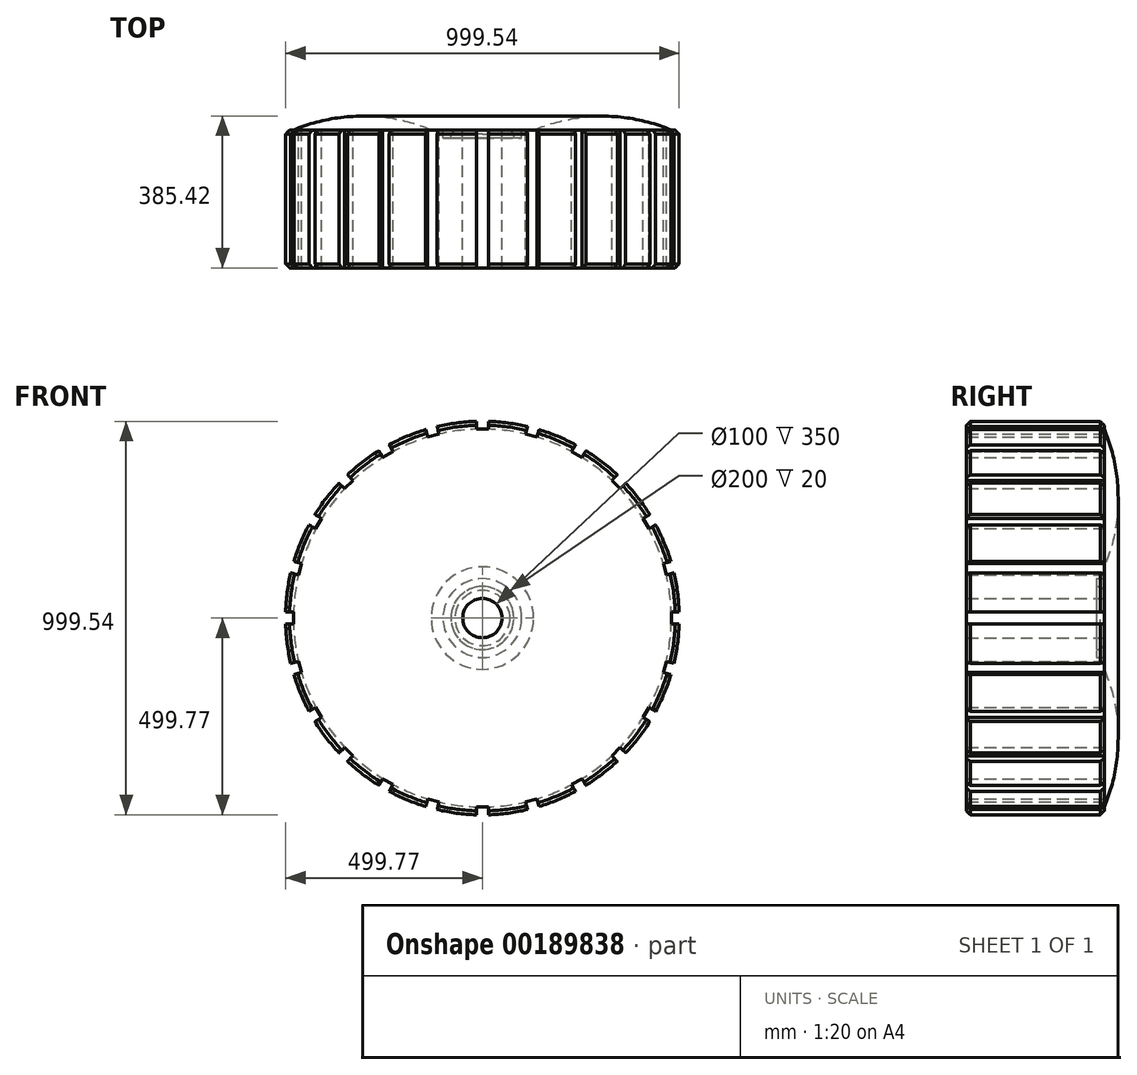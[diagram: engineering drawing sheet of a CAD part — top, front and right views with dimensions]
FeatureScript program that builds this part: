
annotation { "Feature Type Name" : "Feature", "Feature Type Description" : "" }
export const myFeature = defineFeature(function(context is Context, id is Id, definition is map)
    precondition{}
    {
        {
            var Q0;
            Q0=qCreatedBy(makeId("Front.planeOp"),FACE);
            var sketch = newSketch(context, id + "F0", { "sketchPlane" : qUnion([Q0])});
            skCircle(sketch, "E0", {"center": v(0, 0) * mm, "radius": 50 * mm});
            skCircle(sketch, "E1", {"center": v(0, 0) * mm, "radius": 500 * mm});
            skSolve(sketch);
        }
        {
            var Q0;
            Q0=makeQuery(id+"F0.imprint","IMPRINT",FACE,{"disambiguationData":[TD([[makeQuery(id+"F0.imprint","IMPRINT",EDGE,{"derivedFrom":sQuery(id+"F0.wireOp",EDGE,"E0")}),-1.0]])]});
            extrude(context, id + "F1", {"entities" : qUnion([Q0]), "depth" : 350 * mm});
        }
        {
            var Q0;
            Q0=qCreatedBy(makeId("Front.planeOp"),FACE);
            var sketch = newSketch(context, id + "F2", { "sketchPlane" : qUnion([Q0])});
            skLineSegment(sketch, "E2.bottom", {"start": v(15, 500) * mm, "end": v(-15, 500) * mm});
            skLineSegment(sketch, "E2.top", {"start": v(15, 480) * mm, "end": v(-15, 480) * mm});
            skLineSegment(sketch, "E2.left", {"start": v(15, 500) * mm, "end": v(15, 480) * mm});
            skLineSegment(sketch, "E2.right", {"start": v(-15, 500) * mm, "end": v(-15, 480) * mm});
            skLineSegment(sketch, "E3", {"start": v(0, 0) * mm, "end": v(0, 782.63) * mm, "construction": true});
            skLineSegment(sketch, "E4.1.0", {"start": v(-143.9, 479.08) * mm, "end": v(-138.72, 459.76) * mm});
            skLineSegment(sketch, "E4.1.1", {"start": v(-109.74, 467.53) * mm, "end": v(-138.72, 459.76) * mm});
            skLineSegment(sketch, "E4.1.2", {"start": v(-114.92, 486.85) * mm, "end": v(-109.74, 467.53) * mm});
            skLineSegment(sketch, "E4.1.3", {"start": v(-114.92, 486.85) * mm, "end": v(-143.9, 479.08) * mm});
            skLineSegment(sketch, "E4.2.0", {"start": v(-263, 425.51) * mm, "end": v(-253, 408.2) * mm});
            skLineSegment(sketch, "E4.2.1", {"start": v(-227, 423.2) * mm, "end": v(-253, 408.2) * mm});
            skLineSegment(sketch, "E4.2.2", {"start": v(-237, 440.51) * mm, "end": v(-227, 423.2) * mm});
            skLineSegment(sketch, "E4.2.3", {"start": v(-237, 440.51) * mm, "end": v(-263, 425.51) * mm});
            skLineSegment(sketch, "E4.3.0", {"start": v(-364.16, 342.95) * mm, "end": v(-350.02, 328.8) * mm});
            skLineSegment(sketch, "E4.3.1", {"start": v(-328.8, 350.02) * mm, "end": v(-350.02, 328.8) * mm});
            skLineSegment(sketch, "E4.3.2", {"start": v(-342.95, 364.16) * mm, "end": v(-328.8, 350.02) * mm});
            skLineSegment(sketch, "E4.3.3", {"start": v(-342.95, 364.16) * mm, "end": v(-364.16, 342.95) * mm});
            skLineSegment(sketch, "E4.4.0", {"start": v(-440.51, 237) * mm, "end": v(-423.2, 227) * mm});
            skLineSegment(sketch, "E4.4.1", {"start": v(-408.2, 253) * mm, "end": v(-423.2, 227) * mm});
            skLineSegment(sketch, "E4.4.2", {"start": v(-425.51, 263) * mm, "end": v(-408.2, 253) * mm});
            skLineSegment(sketch, "E4.4.3", {"start": v(-425.51, 263) * mm, "end": v(-440.51, 237) * mm});
            skLineSegment(sketch, "E4.5.0", {"start": v(-486.85, 114.92) * mm, "end": v(-467.53, 109.74) * mm});
            skLineSegment(sketch, "E4.5.1", {"start": v(-459.76, 138.72) * mm, "end": v(-467.53, 109.74) * mm});
            skLineSegment(sketch, "E4.5.2", {"start": v(-479.08, 143.9) * mm, "end": v(-459.76, 138.72) * mm});
            skLineSegment(sketch, "E4.5.3", {"start": v(-479.08, 143.9) * mm, "end": v(-486.85, 114.92) * mm});
            skLineSegment(sketch, "E4.6.0", {"start": v(-500, -15) * mm, "end": v(-480, -15) * mm});
            skLineSegment(sketch, "E4.6.1", {"start": v(-480, 15) * mm, "end": v(-480, -15) * mm});
            skLineSegment(sketch, "E4.6.2", {"start": v(-500, 15) * mm, "end": v(-480, 15) * mm});
            skLineSegment(sketch, "E4.6.3", {"start": v(-500, 15) * mm, "end": v(-500, -15) * mm});
            skLineSegment(sketch, "E4.7.0", {"start": v(-479.08, -143.9) * mm, "end": v(-459.76, -138.72) * mm});
            skLineSegment(sketch, "E4.7.1", {"start": v(-467.53, -109.74) * mm, "end": v(-459.76, -138.72) * mm});
            skLineSegment(sketch, "E4.7.2", {"start": v(-486.85, -114.92) * mm, "end": v(-467.53, -109.74) * mm});
            skLineSegment(sketch, "E4.7.3", {"start": v(-486.85, -114.92) * mm, "end": v(-479.08, -143.9) * mm});
            skLineSegment(sketch, "E4.8.0", {"start": v(-425.51, -263) * mm, "end": v(-408.2, -253) * mm});
            skLineSegment(sketch, "E4.8.1", {"start": v(-423.2, -227) * mm, "end": v(-408.2, -253) * mm});
            skLineSegment(sketch, "E4.8.2", {"start": v(-440.51, -237) * mm, "end": v(-423.2, -227) * mm});
            skLineSegment(sketch, "E4.8.3", {"start": v(-440.51, -237) * mm, "end": v(-425.51, -263) * mm});
            skLineSegment(sketch, "E4.9.0", {"start": v(-342.95, -364.16) * mm, "end": v(-328.8, -350.02) * mm});
            skLineSegment(sketch, "E4.9.1", {"start": v(-350.02, -328.8) * mm, "end": v(-328.8, -350.02) * mm});
            skLineSegment(sketch, "E4.9.2", {"start": v(-364.16, -342.95) * mm, "end": v(-350.02, -328.8) * mm});
            skLineSegment(sketch, "E4.9.3", {"start": v(-364.16, -342.95) * mm, "end": v(-342.95, -364.16) * mm});
            skLineSegment(sketch, "E4.10.0", {"start": v(-237, -440.51) * mm, "end": v(-227, -423.2) * mm});
            skLineSegment(sketch, "E4.10.1", {"start": v(-253, -408.2) * mm, "end": v(-227, -423.2) * mm});
            skLineSegment(sketch, "E4.10.2", {"start": v(-263, -425.51) * mm, "end": v(-253, -408.2) * mm});
            skLineSegment(sketch, "E4.10.3", {"start": v(-263, -425.51) * mm, "end": v(-237, -440.51) * mm});
            skLineSegment(sketch, "E4.11.0", {"start": v(-114.92, -486.85) * mm, "end": v(-109.74, -467.53) * mm});
            skLineSegment(sketch, "E4.11.1", {"start": v(-138.72, -459.76) * mm, "end": v(-109.74, -467.53) * mm});
            skLineSegment(sketch, "E4.11.2", {"start": v(-143.9, -479.08) * mm, "end": v(-138.72, -459.76) * mm});
            skLineSegment(sketch, "E4.11.3", {"start": v(-143.9, -479.08) * mm, "end": v(-114.92, -486.85) * mm});
            skLineSegment(sketch, "E4.12.0", {"start": v(15, -500) * mm, "end": v(15, -480) * mm});
            skLineSegment(sketch, "E4.12.1", {"start": v(-15, -480) * mm, "end": v(15, -480) * mm});
            skLineSegment(sketch, "E4.12.2", {"start": v(-15, -500) * mm, "end": v(-15, -480) * mm});
            skLineSegment(sketch, "E4.12.3", {"start": v(-15, -500) * mm, "end": v(15, -500) * mm});
            skLineSegment(sketch, "E4.13.0", {"start": v(143.9, -479.08) * mm, "end": v(138.72, -459.76) * mm});
            skLineSegment(sketch, "E4.13.1", {"start": v(109.74, -467.53) * mm, "end": v(138.72, -459.76) * mm});
            skLineSegment(sketch, "E4.13.2", {"start": v(114.92, -486.85) * mm, "end": v(109.74, -467.53) * mm});
            skLineSegment(sketch, "E4.13.3", {"start": v(114.92, -486.85) * mm, "end": v(143.9, -479.08) * mm});
            skLineSegment(sketch, "E4.14.0", {"start": v(263, -425.51) * mm, "end": v(253, -408.2) * mm});
            skLineSegment(sketch, "E4.14.1", {"start": v(227, -423.2) * mm, "end": v(253, -408.2) * mm});
            skLineSegment(sketch, "E4.14.2", {"start": v(237, -440.51) * mm, "end": v(227, -423.2) * mm});
            skLineSegment(sketch, "E4.14.3", {"start": v(237, -440.51) * mm, "end": v(263, -425.51) * mm});
            skLineSegment(sketch, "E4.15.0", {"start": v(364.16, -342.95) * mm, "end": v(350.02, -328.8) * mm});
            skLineSegment(sketch, "E4.15.1", {"start": v(328.8, -350.02) * mm, "end": v(350.02, -328.8) * mm});
            skLineSegment(sketch, "E4.15.2", {"start": v(342.95, -364.16) * mm, "end": v(328.8, -350.02) * mm});
            skLineSegment(sketch, "E4.15.3", {"start": v(342.95, -364.16) * mm, "end": v(364.16, -342.95) * mm});
            skLineSegment(sketch, "E4.16.0", {"start": v(440.51, -237) * mm, "end": v(423.2, -227) * mm});
            skLineSegment(sketch, "E4.16.1", {"start": v(408.2, -253) * mm, "end": v(423.2, -227) * mm});
            skLineSegment(sketch, "E4.16.2", {"start": v(425.51, -263) * mm, "end": v(408.2, -253) * mm});
            skLineSegment(sketch, "E4.16.3", {"start": v(425.51, -263) * mm, "end": v(440.51, -237) * mm});
            skLineSegment(sketch, "E4.17.0", {"start": v(486.85, -114.92) * mm, "end": v(467.53, -109.74) * mm});
            skLineSegment(sketch, "E4.17.1", {"start": v(459.76, -138.72) * mm, "end": v(467.53, -109.74) * mm});
            skLineSegment(sketch, "E4.17.2", {"start": v(479.08, -143.9) * mm, "end": v(459.76, -138.72) * mm});
            skLineSegment(sketch, "E4.17.3", {"start": v(479.08, -143.9) * mm, "end": v(486.85, -114.92) * mm});
            skLineSegment(sketch, "E4.18.0", {"start": v(500, 15) * mm, "end": v(480, 15) * mm});
            skLineSegment(sketch, "E4.18.1", {"start": v(480, -15) * mm, "end": v(480, 15) * mm});
            skLineSegment(sketch, "E4.18.2", {"start": v(500, -15) * mm, "end": v(480, -15) * mm});
            skLineSegment(sketch, "E4.18.3", {"start": v(500, -15) * mm, "end": v(500, 15) * mm});
            skLineSegment(sketch, "E4.19.0", {"start": v(479.08, 143.9) * mm, "end": v(459.76, 138.72) * mm});
            skLineSegment(sketch, "E4.19.1", {"start": v(467.53, 109.74) * mm, "end": v(459.76, 138.72) * mm});
            skLineSegment(sketch, "E4.19.2", {"start": v(486.85, 114.92) * mm, "end": v(467.53, 109.74) * mm});
            skLineSegment(sketch, "E4.19.3", {"start": v(486.85, 114.92) * mm, "end": v(479.08, 143.9) * mm});
            skLineSegment(sketch, "E4.20.0", {"start": v(425.51, 263) * mm, "end": v(408.2, 253) * mm});
            skLineSegment(sketch, "E4.20.1", {"start": v(423.2, 227) * mm, "end": v(408.2, 253) * mm});
            skLineSegment(sketch, "E4.20.2", {"start": v(440.51, 237) * mm, "end": v(423.2, 227) * mm});
            skLineSegment(sketch, "E4.20.3", {"start": v(440.51, 237) * mm, "end": v(425.51, 263) * mm});
            skLineSegment(sketch, "E4.21.0", {"start": v(342.95, 364.16) * mm, "end": v(328.8, 350.02) * mm});
            skLineSegment(sketch, "E4.21.1", {"start": v(350.02, 328.8) * mm, "end": v(328.8, 350.02) * mm});
            skLineSegment(sketch, "E4.21.2", {"start": v(364.16, 342.95) * mm, "end": v(350.02, 328.8) * mm});
            skLineSegment(sketch, "E4.21.3", {"start": v(364.16, 342.95) * mm, "end": v(342.95, 364.16) * mm});
            skLineSegment(sketch, "E4.22.0", {"start": v(237, 440.51) * mm, "end": v(227, 423.2) * mm});
            skLineSegment(sketch, "E4.22.1", {"start": v(253, 408.2) * mm, "end": v(227, 423.2) * mm});
            skLineSegment(sketch, "E4.22.2", {"start": v(263, 425.51) * mm, "end": v(253, 408.2) * mm});
            skLineSegment(sketch, "E4.22.3", {"start": v(263, 425.51) * mm, "end": v(237, 440.51) * mm});
            skLineSegment(sketch, "E4.23.0", {"start": v(114.92, 486.85) * mm, "end": v(109.74, 467.53) * mm});
            skLineSegment(sketch, "E4.23.1", {"start": v(138.72, 459.76) * mm, "end": v(109.74, 467.53) * mm});
            skLineSegment(sketch, "E4.23.2", {"start": v(143.9, 479.08) * mm, "end": v(138.72, 459.76) * mm});
            skLineSegment(sketch, "E4.23.3", {"start": v(143.9, 479.08) * mm, "end": v(114.92, 486.85) * mm});
            skPoint(sketch, "E4.center", {"position": v(0, 0) * mm});
            skSolve(sketch);
        }
        {
            var Q0;
            Q0=qCreatedBy(makeId("Top.planeOp"),FACE);
            var sketch = newSketch(context, id + "F3", { "sketchPlane" : qUnion([Q0])});
            skArc(sketch, "E5", {"start": v(-130, 0) * mm, "mid": v(-305, 35.42) * mm, "end": v(-480, 0) * mm});
            skLineSegment(sketch, "E6", {"start": v(-130, 0) * mm, "end": v(-480, 0) * mm});
            skSolve(sketch);
        }
        {
            var Q0;
            Q0 = qSketchRegion(id + "F2", true);
            extrude(context, id + "F4", {"entities" : qUnion([Q0]), "operationType" : NewBodyOperationType.REMOVE, "depth" : 1000 * mm, "hasSecondDirection" : true, "secondDirectionOppositeDirection" : true, "secondDirectionDepth" : 350 * mm});
        }
        {
            var Q0;
            Q0=makeQuery(id+"F3.imprint","IMPRINT",FACE,{"disambiguationData":[TD([[makeQuery(id+"F3.imprint","IMPRINT",EDGE,{"derivedFrom":sQuery(id+"F3.wireOp",EDGE,"E5")}),1.0]])]});
            var Q1;
            Q1=makeQuery(id+"F1.opExtrude","SWEPT_FACE",FACE,{"disambiguationData":[OSD([sQuery(id+"F0.wireOp",EDGE,"E0")])]});
            revolve(context, id + "F5", {"operationType" : NewBodyOperationType.ADD, "entities" : qUnion([Q0]), "axis" : qUnion([Q1]), "revolveType" : RevolveType.FULL});
        }
        {
            var Q0;
            {var subQ0=sQuery(id+"F0.wireOp",EDGE,"E0");Q0=makeQuery(id+"F5.boolean.opBoolean","SPLIT",FACE,{"disambiguationData":[TD([makeQuery(id+"F1.opExtrude","SWEPT_FACE",FACE,{"disambiguationData":[OSD([subQ0])]})])],"derivedFrom":makeQuery(id+"F1.opExtrude","CAP_FACE",FACE,{"disambiguationData":[OSD([subQ0,sQuery(id+"F0.wireOp",EDGE,"E1")])],"isStart":true})});}
            var sketch = newSketch(context, id + "F6", { "sketchPlane" : qUnion([Q0])});
            skCircle(sketch, "E7", {"center": v(0, 0) * mm, "radius": 80 * mm});
            skCircle(sketch, "E8", {"center": v(0, 0) * mm, "radius": 100 * mm});
            skSolve(sketch);
        }
        {
            var Q0;
            Q0=makeQuery(id+"F6.imprint","IMPRINT",FACE,{"disambiguationData":[TD([[makeQuery(id+"F6.imprint","IMPRINT",EDGE,{"derivedFrom":sQuery(id+"F6.wireOp",EDGE,"E7")}),-1.0]])]});
            extrude(context, id + "F7", {"entities" : qUnion([Q0]), "operationType" : NewBodyOperationType.REMOVE, "oppositeDirection" : true, "depth" : 20 * mm});
        }
        {
            var Q0;
            {var subQ0=sQuery(id+"F0.wireOp",EDGE,"E1");Q0=makeQuery(id+"F4.boolean.opBoolean","SPLIT",EDGE,{"disambiguationData":[TD([makeQuery(id+"F4.opExtrude","SWEPT_FACE",FACE,{"disambiguationData":[OSD([sQuery(id+"F2.wireOp",EDGE,"E4.20.0")])]})])],"derivedFrom":makeQuery(id+"F1.opExtrude","CAP_EDGE",EDGE,{"disambiguationData":[OSD([subQ0])],"isStart":true})});}
            var Q1;
            {var subQ0=sQuery(id+"F0.wireOp",EDGE,"E1");Q1=makeQuery(id+"F4.boolean.opBoolean","SPLIT",EDGE,{"disambiguationData":[TD([makeQuery(id+"F4.opExtrude","SWEPT_FACE",FACE,{"disambiguationData":[OSD([sQuery(id+"F2.wireOp",EDGE,"E4.19.0")])]})])],"derivedFrom":makeQuery(id+"F1.opExtrude","CAP_EDGE",EDGE,{"disambiguationData":[OSD([subQ0])],"isStart":true})});}
            var Q2;
            {var subQ0=sQuery(id+"F0.wireOp",EDGE,"E1");Q2=makeQuery(id+"F4.boolean.opBoolean","SPLIT",EDGE,{"disambiguationData":[TD([makeQuery(id+"F4.opExtrude","SWEPT_FACE",FACE,{"disambiguationData":[OSD([sQuery(id+"F2.wireOp",EDGE,"E4.18.0")])]})])],"derivedFrom":makeQuery(id+"F1.opExtrude","CAP_EDGE",EDGE,{"disambiguationData":[OSD([subQ0])],"isStart":true})});}
            var Q3;
            {var subQ0=sQuery(id+"F0.wireOp",EDGE,"E1");Q3=makeQuery(id+"F4.boolean.opBoolean","SPLIT",EDGE,{"disambiguationData":[TD([makeQuery(id+"F4.opExtrude","SWEPT_FACE",FACE,{"disambiguationData":[OSD([sQuery(id+"F2.wireOp",EDGE,"E4.21.0")])]})])],"derivedFrom":makeQuery(id+"F1.opExtrude","CAP_EDGE",EDGE,{"disambiguationData":[OSD([subQ0])],"isStart":true})});}
            var Q4;
            {var subQ0=sQuery(id+"F0.wireOp",EDGE,"E1");Q4=makeQuery(id+"F4.boolean.opBoolean","SPLIT",EDGE,{"disambiguationData":[TD([makeQuery(id+"F4.opExtrude","SWEPT_FACE",FACE,{"disambiguationData":[OSD([sQuery(id+"F2.wireOp",EDGE,"E4.22.0")])]})])],"derivedFrom":makeQuery(id+"F1.opExtrude","CAP_EDGE",EDGE,{"disambiguationData":[OSD([subQ0])],"isStart":true})});}
            var Q5;
            {var subQ0=sQuery(id+"F0.wireOp",EDGE,"E1");Q5=makeQuery(id+"F4.boolean.opBoolean","SPLIT",EDGE,{"disambiguationData":[TD([makeQuery(id+"F4.opExtrude","SWEPT_FACE",FACE,{"disambiguationData":[OSD([sQuery(id+"F2.wireOp",EDGE,"E2.left")])]})])],"derivedFrom":makeQuery(id+"F1.opExtrude","CAP_EDGE",EDGE,{"disambiguationData":[OSD([subQ0])],"isStart":true})});}
            var Q6;
            {var subQ0=sQuery(id+"F0.wireOp",EDGE,"E1");Q6=makeQuery(id+"F4.boolean.opBoolean","SPLIT",EDGE,{"disambiguationData":[TD([makeQuery(id+"F4.opExtrude","SWEPT_FACE",FACE,{"disambiguationData":[OSD([sQuery(id+"F2.wireOp",EDGE,"E2.right")])]})])],"derivedFrom":makeQuery(id+"F1.opExtrude","CAP_EDGE",EDGE,{"disambiguationData":[OSD([subQ0])],"isStart":true})});}
            var Q7;
            {var subQ0=sQuery(id+"F0.wireOp",EDGE,"E1");Q7=makeQuery(id+"F4.boolean.opBoolean","SPLIT",EDGE,{"disambiguationData":[TD([makeQuery(id+"F4.opExtrude","SWEPT_FACE",FACE,{"disambiguationData":[OSD([sQuery(id+"F2.wireOp",EDGE,"E4.1.0")])]})])],"derivedFrom":makeQuery(id+"F1.opExtrude","CAP_EDGE",EDGE,{"disambiguationData":[OSD([subQ0])],"isStart":true})});}
            var Q8;
            {var subQ0=sQuery(id+"F0.wireOp",EDGE,"E1");Q8=makeQuery(id+"F4.boolean.opBoolean","SPLIT",EDGE,{"disambiguationData":[TD([makeQuery(id+"F4.opExtrude","SWEPT_FACE",FACE,{"disambiguationData":[OSD([sQuery(id+"F2.wireOp",EDGE,"E4.2.0")])]})])],"derivedFrom":makeQuery(id+"F1.opExtrude","CAP_EDGE",EDGE,{"disambiguationData":[OSD([subQ0])],"isStart":true})});}
            var Q9;
            {var subQ0=sQuery(id+"F0.wireOp",EDGE,"E1");Q9=makeQuery(id+"F4.boolean.opBoolean","SPLIT",EDGE,{"disambiguationData":[TD([makeQuery(id+"F4.opExtrude","SWEPT_FACE",FACE,{"disambiguationData":[OSD([sQuery(id+"F2.wireOp",EDGE,"E4.3.0")])]})])],"derivedFrom":makeQuery(id+"F1.opExtrude","CAP_EDGE",EDGE,{"disambiguationData":[OSD([subQ0])],"isStart":true})});}
            var Q10;
            {var subQ0=sQuery(id+"F0.wireOp",EDGE,"E1");Q10=makeQuery(id+"F4.boolean.opBoolean","SPLIT",EDGE,{"disambiguationData":[TD([makeQuery(id+"F4.opExtrude","SWEPT_FACE",FACE,{"disambiguationData":[OSD([sQuery(id+"F2.wireOp",EDGE,"E4.4.0")])]})])],"derivedFrom":makeQuery(id+"F1.opExtrude","CAP_EDGE",EDGE,{"disambiguationData":[OSD([subQ0])],"isStart":true})});}
            var Q11;
            {var subQ0=sQuery(id+"F0.wireOp",EDGE,"E1");Q11=makeQuery(id+"F4.boolean.opBoolean","SPLIT",EDGE,{"disambiguationData":[TD([makeQuery(id+"F4.opExtrude","SWEPT_FACE",FACE,{"disambiguationData":[OSD([sQuery(id+"F2.wireOp",EDGE,"E4.5.0")])]})])],"derivedFrom":makeQuery(id+"F1.opExtrude","CAP_EDGE",EDGE,{"disambiguationData":[OSD([subQ0])],"isStart":true})});}
            var Q12;
            {var subQ0=sQuery(id+"F0.wireOp",EDGE,"E1");Q12=makeQuery(id+"F4.boolean.opBoolean","SPLIT",EDGE,{"disambiguationData":[TD([makeQuery(id+"F4.opExtrude","SWEPT_FACE",FACE,{"disambiguationData":[OSD([sQuery(id+"F2.wireOp",EDGE,"E4.21.0")])]})])],"derivedFrom":makeQuery(id+"F1.opExtrude","CAP_EDGE",EDGE,{"disambiguationData":[OSD([subQ0])],"isStart":false})});}
            var Q13;
            {var subQ0=sQuery(id+"F0.wireOp",EDGE,"E1");Q13=makeQuery(id+"F4.boolean.opBoolean","SPLIT",EDGE,{"disambiguationData":[TD([makeQuery(id+"F4.opExtrude","SWEPT_FACE",FACE,{"disambiguationData":[OSD([sQuery(id+"F2.wireOp",EDGE,"E4.22.0")])]})])],"derivedFrom":makeQuery(id+"F1.opExtrude","CAP_EDGE",EDGE,{"disambiguationData":[OSD([subQ0])],"isStart":false})});}
            var Q14;
            {var subQ0=sQuery(id+"F0.wireOp",EDGE,"E1");Q14=makeQuery(id+"F4.boolean.opBoolean","SPLIT",EDGE,{"disambiguationData":[TD([makeQuery(id+"F4.opExtrude","SWEPT_FACE",FACE,{"disambiguationData":[OSD([sQuery(id+"F2.wireOp",EDGE,"E4.20.0")])]})])],"derivedFrom":makeQuery(id+"F1.opExtrude","CAP_EDGE",EDGE,{"disambiguationData":[OSD([subQ0])],"isStart":false})});}
            var Q15;
            {var subQ0=sQuery(id+"F0.wireOp",EDGE,"E1");Q15=makeQuery(id+"F4.boolean.opBoolean","SPLIT",EDGE,{"disambiguationData":[TD([makeQuery(id+"F4.opExtrude","SWEPT_FACE",FACE,{"disambiguationData":[OSD([sQuery(id+"F2.wireOp",EDGE,"E2.left")])]})])],"derivedFrom":makeQuery(id+"F1.opExtrude","CAP_EDGE",EDGE,{"disambiguationData":[OSD([subQ0])],"isStart":false})});}
            var Q16;
            {var subQ0=sQuery(id+"F0.wireOp",EDGE,"E1");Q16=makeQuery(id+"F4.boolean.opBoolean","SPLIT",EDGE,{"disambiguationData":[TD([makeQuery(id+"F4.opExtrude","SWEPT_FACE",FACE,{"disambiguationData":[OSD([sQuery(id+"F2.wireOp",EDGE,"E4.17.0")])]})])],"derivedFrom":makeQuery(id+"F1.opExtrude","CAP_EDGE",EDGE,{"disambiguationData":[OSD([subQ0])],"isStart":true})});}
            var Q17;
            {var subQ0=sQuery(id+"F0.wireOp",EDGE,"E1");Q17=makeQuery(id+"F4.boolean.opBoolean","SPLIT",EDGE,{"disambiguationData":[TD([makeQuery(id+"F4.opExtrude","SWEPT_FACE",FACE,{"disambiguationData":[OSD([sQuery(id+"F2.wireOp",EDGE,"E4.16.0")])]})])],"derivedFrom":makeQuery(id+"F1.opExtrude","CAP_EDGE",EDGE,{"disambiguationData":[OSD([subQ0])],"isStart":true})});}
            var Q18;
            {var subQ0=sQuery(id+"F0.wireOp",EDGE,"E1");Q18=makeQuery(id+"F4.boolean.opBoolean","SPLIT",EDGE,{"disambiguationData":[TD([makeQuery(id+"F4.opExtrude","SWEPT_FACE",FACE,{"disambiguationData":[OSD([sQuery(id+"F2.wireOp",EDGE,"E4.18.0")])]})])],"derivedFrom":makeQuery(id+"F1.opExtrude","CAP_EDGE",EDGE,{"disambiguationData":[OSD([subQ0])],"isStart":false})});}
            var Q19;
            {var subQ0=sQuery(id+"F0.wireOp",EDGE,"E1");Q19=makeQuery(id+"F4.boolean.opBoolean","SPLIT",EDGE,{"disambiguationData":[TD([makeQuery(id+"F4.opExtrude","SWEPT_FACE",FACE,{"disambiguationData":[OSD([sQuery(id+"F2.wireOp",EDGE,"E4.19.0")])]})])],"derivedFrom":makeQuery(id+"F1.opExtrude","CAP_EDGE",EDGE,{"disambiguationData":[OSD([subQ0])],"isStart":false})});}
            var Q20;
            {var subQ0=sQuery(id+"F0.wireOp",EDGE,"E1");Q20=makeQuery(id+"F4.boolean.opBoolean","SPLIT",EDGE,{"disambiguationData":[TD([makeQuery(id+"F4.opExtrude","SWEPT_FACE",FACE,{"disambiguationData":[OSD([sQuery(id+"F2.wireOp",EDGE,"E4.17.0")])]})])],"derivedFrom":makeQuery(id+"F1.opExtrude","CAP_EDGE",EDGE,{"disambiguationData":[OSD([subQ0])],"isStart":false})});}
            var Q21;
            {var subQ0=sQuery(id+"F0.wireOp",EDGE,"E1");Q21=makeQuery(id+"F4.boolean.opBoolean","SPLIT",EDGE,{"disambiguationData":[TD([makeQuery(id+"F4.opExtrude","SWEPT_FACE",FACE,{"disambiguationData":[OSD([sQuery(id+"F2.wireOp",EDGE,"E4.16.0")])]})])],"derivedFrom":makeQuery(id+"F1.opExtrude","CAP_EDGE",EDGE,{"disambiguationData":[OSD([subQ0])],"isStart":false})});}
            var Q22;
            {var subQ0=sQuery(id+"F0.wireOp",EDGE,"E1");Q22=makeQuery(id+"F4.boolean.opBoolean","SPLIT",EDGE,{"disambiguationData":[TD([makeQuery(id+"F4.opExtrude","SWEPT_FACE",FACE,{"disambiguationData":[OSD([sQuery(id+"F2.wireOp",EDGE,"E4.15.0")])]})])],"derivedFrom":makeQuery(id+"F1.opExtrude","CAP_EDGE",EDGE,{"disambiguationData":[OSD([subQ0])],"isStart":false})});}
            var Q23;
            {var subQ0=sQuery(id+"F0.wireOp",EDGE,"E1");Q23=makeQuery(id+"F4.boolean.opBoolean","SPLIT",EDGE,{"disambiguationData":[TD([makeQuery(id+"F4.opExtrude","SWEPT_FACE",FACE,{"disambiguationData":[OSD([sQuery(id+"F2.wireOp",EDGE,"E4.15.0")])]})])],"derivedFrom":makeQuery(id+"F1.opExtrude","CAP_EDGE",EDGE,{"disambiguationData":[OSD([subQ0])],"isStart":true})});}
            var Q24;
            {var subQ0=sQuery(id+"F0.wireOp",EDGE,"E1");Q24=makeQuery(id+"F4.boolean.opBoolean","SPLIT",EDGE,{"disambiguationData":[TD([makeQuery(id+"F4.opExtrude","SWEPT_FACE",FACE,{"disambiguationData":[OSD([sQuery(id+"F2.wireOp",EDGE,"E4.14.0")])]})])],"derivedFrom":makeQuery(id+"F1.opExtrude","CAP_EDGE",EDGE,{"disambiguationData":[OSD([subQ0])],"isStart":false})});}
            var Q25;
            {var subQ0=sQuery(id+"F0.wireOp",EDGE,"E1");Q25=makeQuery(id+"F4.boolean.opBoolean","SPLIT",EDGE,{"disambiguationData":[TD([makeQuery(id+"F4.opExtrude","SWEPT_FACE",FACE,{"disambiguationData":[OSD([sQuery(id+"F2.wireOp",EDGE,"E4.14.0")])]})])],"derivedFrom":makeQuery(id+"F1.opExtrude","CAP_EDGE",EDGE,{"disambiguationData":[OSD([subQ0])],"isStart":true})});}
            var Q26;
            {var subQ0=sQuery(id+"F0.wireOp",EDGE,"E1");Q26=makeQuery(id+"F4.boolean.opBoolean","SPLIT",EDGE,{"disambiguationData":[TD([makeQuery(id+"F4.opExtrude","SWEPT_FACE",FACE,{"disambiguationData":[OSD([sQuery(id+"F2.wireOp",EDGE,"E4.13.0")])]})])],"derivedFrom":makeQuery(id+"F1.opExtrude","CAP_EDGE",EDGE,{"disambiguationData":[OSD([subQ0])],"isStart":false})});}
            var Q27;
            {var subQ0=sQuery(id+"F0.wireOp",EDGE,"E1");Q27=makeQuery(id+"F4.boolean.opBoolean","SPLIT",EDGE,{"disambiguationData":[TD([makeQuery(id+"F4.opExtrude","SWEPT_FACE",FACE,{"disambiguationData":[OSD([sQuery(id+"F2.wireOp",EDGE,"E4.13.0")])]})])],"derivedFrom":makeQuery(id+"F1.opExtrude","CAP_EDGE",EDGE,{"disambiguationData":[OSD([subQ0])],"isStart":true})});}
            var Q28;
            {var subQ0=sQuery(id+"F0.wireOp",EDGE,"E1");Q28=makeQuery(id+"F4.boolean.opBoolean","SPLIT",EDGE,{"disambiguationData":[TD([makeQuery(id+"F4.opExtrude","SWEPT_FACE",FACE,{"disambiguationData":[OSD([sQuery(id+"F2.wireOp",EDGE,"E4.12.0")])]})])],"derivedFrom":makeQuery(id+"F1.opExtrude","CAP_EDGE",EDGE,{"disambiguationData":[OSD([subQ0])],"isStart":true})});}
            var Q29;
            {var subQ0=sQuery(id+"F0.wireOp",EDGE,"E1");Q29=makeQuery(id+"F4.boolean.opBoolean","SPLIT",EDGE,{"disambiguationData":[TD([makeQuery(id+"F4.opExtrude","SWEPT_FACE",FACE,{"disambiguationData":[OSD([sQuery(id+"F2.wireOp",EDGE,"E4.12.0")])]})])],"derivedFrom":makeQuery(id+"F1.opExtrude","CAP_EDGE",EDGE,{"disambiguationData":[OSD([subQ0])],"isStart":false})});}
            var Q30;
            {var subQ0=sQuery(id+"F0.wireOp",EDGE,"E1");Q30=makeQuery(id+"F4.boolean.opBoolean","SPLIT",EDGE,{"disambiguationData":[TD([makeQuery(id+"F4.opExtrude","SWEPT_FACE",FACE,{"disambiguationData":[OSD([sQuery(id+"F2.wireOp",EDGE,"E4.11.0")])]})])],"derivedFrom":makeQuery(id+"F1.opExtrude","CAP_EDGE",EDGE,{"disambiguationData":[OSD([subQ0])],"isStart":false})});}
            var Q31;
            {var subQ0=sQuery(id+"F0.wireOp",EDGE,"E1");Q31=makeQuery(id+"F4.boolean.opBoolean","SPLIT",EDGE,{"disambiguationData":[TD([makeQuery(id+"F4.opExtrude","SWEPT_FACE",FACE,{"disambiguationData":[OSD([sQuery(id+"F2.wireOp",EDGE,"E4.10.0")])]})])],"derivedFrom":makeQuery(id+"F1.opExtrude","CAP_EDGE",EDGE,{"disambiguationData":[OSD([subQ0])],"isStart":false})});}
            var Q32;
            {var subQ0=sQuery(id+"F0.wireOp",EDGE,"E1");Q32=makeQuery(id+"F4.boolean.opBoolean","SPLIT",EDGE,{"disambiguationData":[TD([makeQuery(id+"F4.opExtrude","SWEPT_FACE",FACE,{"disambiguationData":[OSD([sQuery(id+"F2.wireOp",EDGE,"E4.11.0")])]})])],"derivedFrom":makeQuery(id+"F1.opExtrude","CAP_EDGE",EDGE,{"disambiguationData":[OSD([subQ0])],"isStart":true})});}
            var Q33;
            {var subQ0=sQuery(id+"F0.wireOp",EDGE,"E1");Q33=makeQuery(id+"F4.boolean.opBoolean","SPLIT",EDGE,{"disambiguationData":[TD([makeQuery(id+"F4.opExtrude","SWEPT_FACE",FACE,{"disambiguationData":[OSD([sQuery(id+"F2.wireOp",EDGE,"E4.10.0")])]})])],"derivedFrom":makeQuery(id+"F1.opExtrude","CAP_EDGE",EDGE,{"disambiguationData":[OSD([subQ0])],"isStart":true})});}
            var Q34;
            {var subQ0=sQuery(id+"F0.wireOp",EDGE,"E1");Q34=makeQuery(id+"F4.boolean.opBoolean","SPLIT",EDGE,{"disambiguationData":[TD([makeQuery(id+"F4.opExtrude","SWEPT_FACE",FACE,{"disambiguationData":[OSD([sQuery(id+"F2.wireOp",EDGE,"E4.9.0")])]})])],"derivedFrom":makeQuery(id+"F1.opExtrude","CAP_EDGE",EDGE,{"disambiguationData":[OSD([subQ0])],"isStart":true})});}
            var Q35;
            {var subQ0=sQuery(id+"F0.wireOp",EDGE,"E1");Q35=makeQuery(id+"F4.boolean.opBoolean","SPLIT",EDGE,{"disambiguationData":[TD([makeQuery(id+"F4.opExtrude","SWEPT_FACE",FACE,{"disambiguationData":[OSD([sQuery(id+"F2.wireOp",EDGE,"E4.8.0")])]})])],"derivedFrom":makeQuery(id+"F1.opExtrude","CAP_EDGE",EDGE,{"disambiguationData":[OSD([subQ0])],"isStart":true})});}
            var Q36;
            {var subQ0=sQuery(id+"F0.wireOp",EDGE,"E1");Q36=makeQuery(id+"F4.boolean.opBoolean","SPLIT",EDGE,{"disambiguationData":[TD([makeQuery(id+"F4.opExtrude","SWEPT_FACE",FACE,{"disambiguationData":[OSD([sQuery(id+"F2.wireOp",EDGE,"E4.9.0")])]})])],"derivedFrom":makeQuery(id+"F1.opExtrude","CAP_EDGE",EDGE,{"disambiguationData":[OSD([subQ0])],"isStart":false})});}
            var Q37;
            {var subQ0=sQuery(id+"F0.wireOp",EDGE,"E1");Q37=makeQuery(id+"F4.boolean.opBoolean","SPLIT",EDGE,{"disambiguationData":[TD([makeQuery(id+"F4.opExtrude","SWEPT_FACE",FACE,{"disambiguationData":[OSD([sQuery(id+"F2.wireOp",EDGE,"E4.8.0")])]})])],"derivedFrom":makeQuery(id+"F1.opExtrude","CAP_EDGE",EDGE,{"disambiguationData":[OSD([subQ0])],"isStart":false})});}
            var Q38;
            {var subQ0=sQuery(id+"F0.wireOp",EDGE,"E1");Q38=makeQuery(id+"F4.boolean.opBoolean","SPLIT",EDGE,{"disambiguationData":[TD([makeQuery(id+"F4.opExtrude","SWEPT_FACE",FACE,{"disambiguationData":[OSD([sQuery(id+"F2.wireOp",EDGE,"E4.6.0")])]})])],"derivedFrom":makeQuery(id+"F1.opExtrude","CAP_EDGE",EDGE,{"disambiguationData":[OSD([subQ0])],"isStart":true})});}
            var Q39;
            {var subQ0=sQuery(id+"F0.wireOp",EDGE,"E1");Q39=makeQuery(id+"F4.boolean.opBoolean","SPLIT",EDGE,{"disambiguationData":[TD([makeQuery(id+"F4.opExtrude","SWEPT_FACE",FACE,{"disambiguationData":[OSD([sQuery(id+"F2.wireOp",EDGE,"E4.7.0")])]})])],"derivedFrom":makeQuery(id+"F1.opExtrude","CAP_EDGE",EDGE,{"disambiguationData":[OSD([subQ0])],"isStart":false})});}
            var Q40;
            {var subQ0=sQuery(id+"F0.wireOp",EDGE,"E1");Q40=makeQuery(id+"F4.boolean.opBoolean","SPLIT",EDGE,{"disambiguationData":[TD([makeQuery(id+"F4.opExtrude","SWEPT_FACE",FACE,{"disambiguationData":[OSD([sQuery(id+"F2.wireOp",EDGE,"E4.6.0")])]})])],"derivedFrom":makeQuery(id+"F1.opExtrude","CAP_EDGE",EDGE,{"disambiguationData":[OSD([subQ0])],"isStart":false})});}
            var Q41;
            {var subQ0=sQuery(id+"F0.wireOp",EDGE,"E1");Q41=makeQuery(id+"F4.boolean.opBoolean","SPLIT",EDGE,{"disambiguationData":[TD([makeQuery(id+"F4.opExtrude","SWEPT_FACE",FACE,{"disambiguationData":[OSD([sQuery(id+"F2.wireOp",EDGE,"E4.5.0")])]})])],"derivedFrom":makeQuery(id+"F1.opExtrude","CAP_EDGE",EDGE,{"disambiguationData":[OSD([subQ0])],"isStart":false})});}
            var Q42;
            {var subQ0=sQuery(id+"F0.wireOp",EDGE,"E1");Q42=makeQuery(id+"F4.boolean.opBoolean","SPLIT",EDGE,{"disambiguationData":[TD([makeQuery(id+"F4.opExtrude","SWEPT_FACE",FACE,{"disambiguationData":[OSD([sQuery(id+"F2.wireOp",EDGE,"E4.4.0")])]})])],"derivedFrom":makeQuery(id+"F1.opExtrude","CAP_EDGE",EDGE,{"disambiguationData":[OSD([subQ0])],"isStart":false})});}
            var Q43;
            {var subQ0=sQuery(id+"F0.wireOp",EDGE,"E1");Q43=makeQuery(id+"F4.boolean.opBoolean","SPLIT",EDGE,{"disambiguationData":[TD([makeQuery(id+"F4.opExtrude","SWEPT_FACE",FACE,{"disambiguationData":[OSD([sQuery(id+"F2.wireOp",EDGE,"E4.7.0")])]})])],"derivedFrom":makeQuery(id+"F1.opExtrude","CAP_EDGE",EDGE,{"disambiguationData":[OSD([subQ0])],"isStart":true})});}
            var Q44;
            {var subQ0=sQuery(id+"F0.wireOp",EDGE,"E1");Q44=makeQuery(id+"F4.boolean.opBoolean","SPLIT",EDGE,{"disambiguationData":[TD([makeQuery(id+"F4.opExtrude","SWEPT_FACE",FACE,{"disambiguationData":[OSD([sQuery(id+"F2.wireOp",EDGE,"E4.7.0")])]})])],"derivedFrom":makeQuery(id+"F1.opExtrude","CAP_EDGE",EDGE,{"disambiguationData":[OSD([subQ0])],"isStart":true})});}
            var Q45;
            {var subQ0=sQuery(id+"F0.wireOp",EDGE,"E1");Q45=makeQuery(id+"F4.boolean.opBoolean","SPLIT",EDGE,{"disambiguationData":[TD([makeQuery(id+"F4.opExtrude","SWEPT_FACE",FACE,{"disambiguationData":[OSD([sQuery(id+"F2.wireOp",EDGE,"E2.right")])]})])],"derivedFrom":makeQuery(id+"F1.opExtrude","CAP_EDGE",EDGE,{"disambiguationData":[OSD([subQ0])],"isStart":false})});}
            var Q46;
            {var subQ0=sQuery(id+"F0.wireOp",EDGE,"E1");Q46=makeQuery(id+"F4.boolean.opBoolean","SPLIT",EDGE,{"disambiguationData":[TD([makeQuery(id+"F4.opExtrude","SWEPT_FACE",FACE,{"disambiguationData":[OSD([sQuery(id+"F2.wireOp",EDGE,"E4.1.0")])]})])],"derivedFrom":makeQuery(id+"F1.opExtrude","CAP_EDGE",EDGE,{"disambiguationData":[OSD([subQ0])],"isStart":false})});}
            var Q47;
            {var subQ0=sQuery(id+"F0.wireOp",EDGE,"E1");Q47=makeQuery(id+"F4.boolean.opBoolean","SPLIT",EDGE,{"disambiguationData":[TD([makeQuery(id+"F4.opExtrude","SWEPT_FACE",FACE,{"disambiguationData":[OSD([sQuery(id+"F2.wireOp",EDGE,"E4.2.0")])]})])],"derivedFrom":makeQuery(id+"F1.opExtrude","CAP_EDGE",EDGE,{"disambiguationData":[OSD([subQ0])],"isStart":false})});}
            var Q48;
            {var subQ0=sQuery(id+"F0.wireOp",EDGE,"E1");Q48=makeQuery(id+"F4.boolean.opBoolean","SPLIT",EDGE,{"disambiguationData":[TD([makeQuery(id+"F4.opExtrude","SWEPT_FACE",FACE,{"disambiguationData":[OSD([sQuery(id+"F2.wireOp",EDGE,"E4.3.0")])]})])],"derivedFrom":makeQuery(id+"F1.opExtrude","CAP_EDGE",EDGE,{"disambiguationData":[OSD([subQ0])],"isStart":false})});}
            chamfer(context, id + "F8", {"entities" : qUnion([Q0, Q1, Q2, Q3, Q4, Q5, Q6, Q7, Q8, Q9, Q10, Q11, Q12, Q13, Q14, Q15, Q16, Q17, Q18, Q19, Q20, Q21, Q22, Q23, Q24, Q25, Q26, Q27, Q28, Q29, Q30, Q31, Q32, Q33, Q34, Q35, Q36, Q37, Q38, Q39, Q40, Q41, Q42, Q43, Q44, Q45, Q46, Q47, Q48]), "width" : 10 * mm, "tangentPropagation" : true});
        }
        {
            var Q0;
            Q0=makeQuery(id+"F7.boolean.opBoolean","COPY",EDGE,{"derivedFrom":makeQuery(id+"F7.opExtrude","CAP_EDGE",EDGE,{"disambiguationData":[OSD([sQuery(id+"F6.wireOp",EDGE,"E8")])],"isStart":true})});
            var Q1;
            Q1=makeQuery(id+"F7.boolean.opBoolean","COPY",EDGE,{"derivedFrom":makeQuery(id+"F7.opExtrude","CAP_EDGE",EDGE,{"disambiguationData":[OSD([sQuery(id+"F6.wireOp",EDGE,"E7")])],"isStart":true})});
            chamfer(context, id + "F9", {"entities" : qUnion([Q0, Q1]), "width" : 10 * mm, "tangentPropagation" : true});
        }
    });
